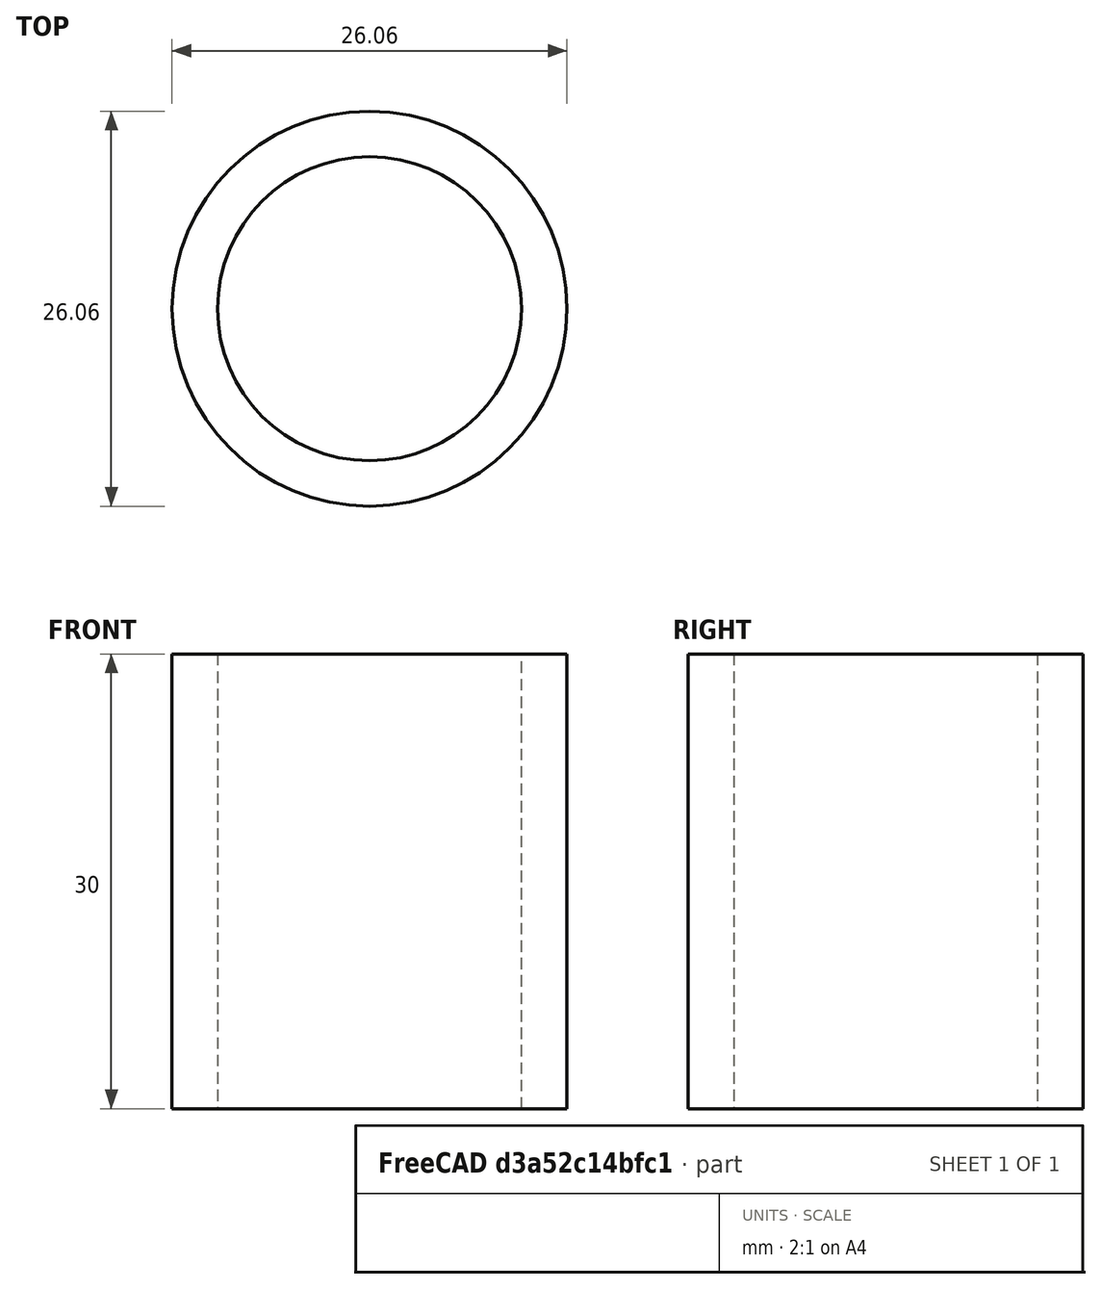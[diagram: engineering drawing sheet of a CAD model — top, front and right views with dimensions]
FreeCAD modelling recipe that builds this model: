
FCSTD DOCUMENT  (FreeCAD 0.19R23074 (Git))
Label: giunzione
License: All rights reserved
LicenseURL: http://en.wikipedia.org/wiki/All_rights_reserved
objects: Sketcher::SketchObject×1, PartDesign::Pad×1, PartDesign::Body×1
note: 4 computed .brp shape members not serialized (recipe doc carries the construction recipe); baked Part::Feature solids carry a one-line shape summary decoded from their .brp

FEATURE [Sketcher::SketchObject] Sketch
  MapMode = 5
  Support = -> [XY_Plane]
  sketch-geometry (2):
    g0: Circle CenterX=0 CenterY=0 CenterZ=0 NormalX=0 NormalY=0 NormalZ=1 AngleXU=0 Radius=10.03
    g1: Circle CenterX=0 CenterY=0 CenterZ=0 NormalX=0 NormalY=0 NormalZ=1 AngleXU=0 Radius=13.03
  constraints (4):
    c: Coincident(g0,g-1)
    c: Radius(g0) = 10.03
    c: Coincident(g1,g0)
    c: Radius(g1) = 13.03
FEATURE [PartDesign::Pad] Pad
  Direction = (1,1,1)
  Length = 30
  Length2 = 100
  Profile = -> Sketch
  Type = 0
FEATURE [PartDesign::Body] Body
  Group = -> [Sketch,Pad]
  Origin = -> Origin
  Tip = -> Pad
